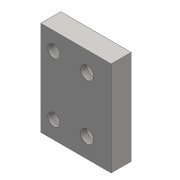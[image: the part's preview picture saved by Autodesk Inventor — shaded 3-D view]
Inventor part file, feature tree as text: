
AUTODESK INVENTOR PART (.ipt)
format: ipt  version: 2016 (Build 200138000, 138)  size: 928,768 bytes
history: native  units: mm
features: sketch x4, extrude x2, hole x2, chamfer x1, mirror x1, projected_geometry x1
ambient origin geometry x8: Origin, YZ Plane, XZ Plane, XY Plane, X Axis, Y Axis, Z Axis, Center Point
bodies: Body1 (feature_tree)
feature tree (11):
  sketch  "Sketch1"  dims[d5=4.8mm d6=4.8mm]
  extrude  "Extrusion3"  Depth=4.8mm
  chamfer  "Chamfer2"  Distance=3.0mm
  extrude  "Extrusion4"  Depth=3.0mm
  hole  "Hole1"  [1 undecoded]
  hole  "Hole3"  [1 undecoded]
  mirror  "Mirror1"
  sketch  "Sketch3"  dims[d7=3.0mm]
  sketch  "Sketch5"  dims[d8=3.0mm]
  projected_geometry  "Projected Loop1"
  sketch  "Sketch7"  dims[d9=3.0mm d10=3.0mm d11=3.0mm d12=3.0mm d17=4.25mm d19=1.5mm d20=4.3mm d21=10.0mm d22=2.0mm d23=1.5mm d24=4.3mm d25=10.0mm d26=2.0mm d35=0.5mm d37=1.5mm d48=1.0mm d52=2.0mm d53=0.0mm d54=0.2mm d55=2.0mm d56=45.0deg d60=10.0mm d63=5.0mm d64=0.0mm d65=4.0mm d66=0.0mm d67=3.2mm d68=6.0mm d69=6.0mm d70=3.5mm d71=90.0deg d72=8.0mm d73=20.594885mm d74=0.0mm d75=2.0mm d83=3.0mm d84=6.0mm d85=6.0mm d86=3.5mm d87=90.0deg d88=8.0mm d89=20.594885mm d90=0.2mm d91=0.2mm d92=0.2mm d93=0.2mm d94=0.2mm d95=0.2mm]
note: 2 required parameter values undecoded (feature->parameter linkage not recoverable at this tier; creation-order binding heuristic only, values carry confidence <= 0.55)
